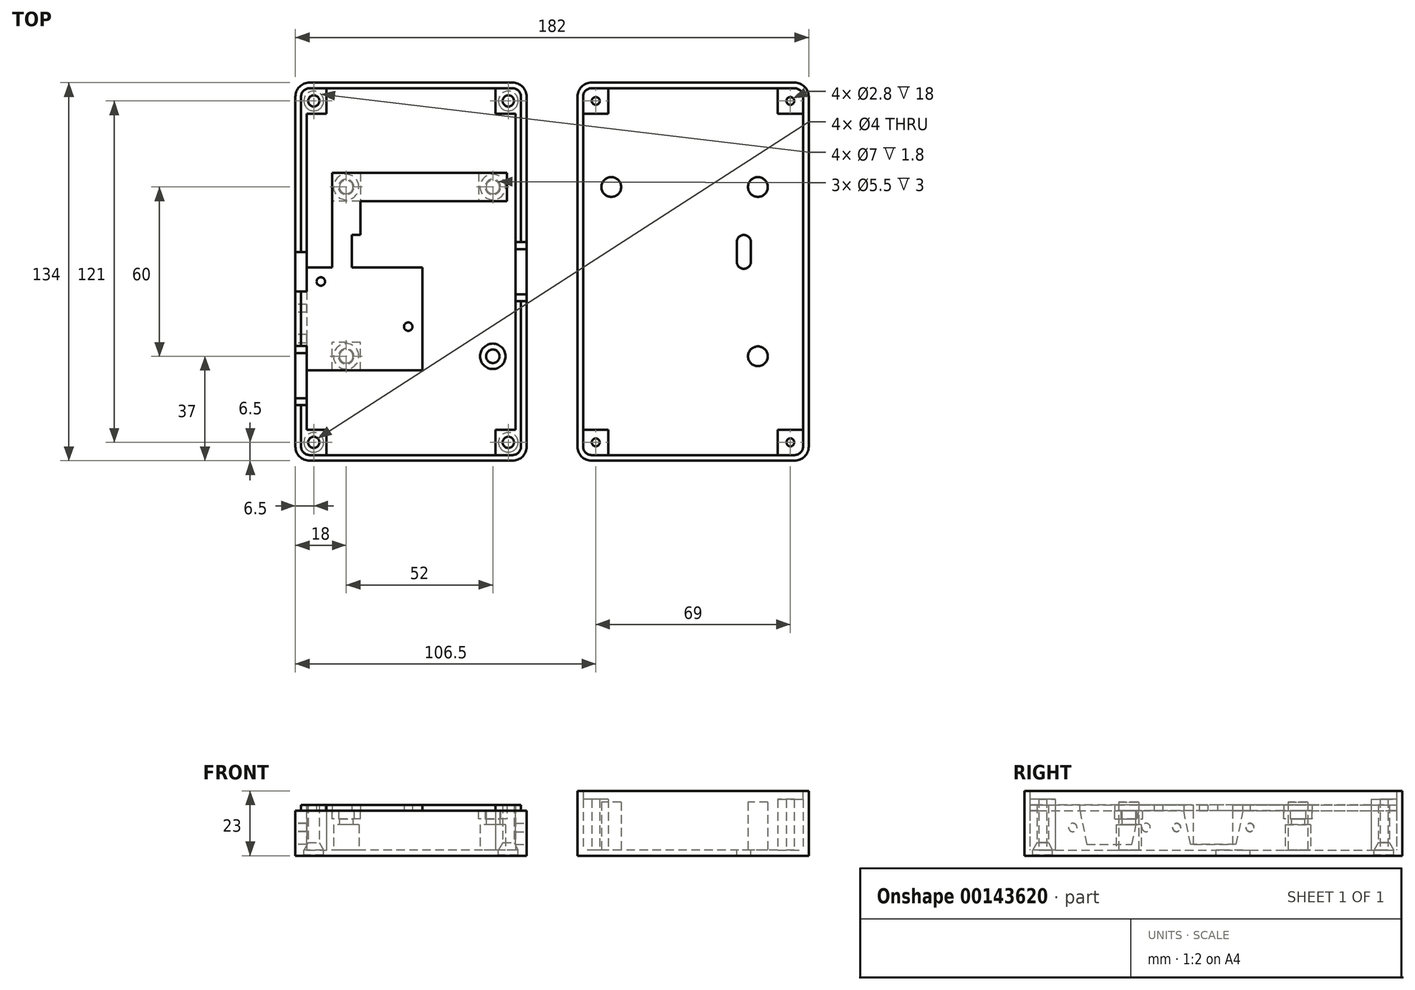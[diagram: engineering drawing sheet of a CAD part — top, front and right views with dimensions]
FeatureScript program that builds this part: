
annotation { "Feature Type Name" : "Feature", "Feature Type Description" : "" }
export const myFeature = defineFeature(function(context is Context, id is Id, definition is map)
    precondition{}
    {
        {
            var Q0;
            Q0=qCreatedBy(makeId("Top.planeOp"),FACE);
            var sketch = newSketch(context, id + "F0", { "sketchPlane" : qUnion([Q0])});
            skLineSegment(sketch, "E0.bottom", {"start": v(36, -67) * mm, "end": v(-36, -67) * mm});
            skLineSegment(sketch, "E0.top", {"start": v(36, 67) * mm, "end": v(-36, 67) * mm});
            skLineSegment(sketch, "E0.left", {"start": v(41, -62) * mm, "end": v(41, 62) * mm});
            skLineSegment(sketch, "E0.right", {"start": v(-41, -62) * mm, "end": v(-41, 62) * mm});
            skPoint(sketch, "E0.middle", {"position": v(0, 0) * mm});
            skPoint(sketch, "E1.visualSharp", {"position": v(41, 67) * mm});
            skArc(sketch, "E1.filletArc", {"start": v(41, 62) * mm, "mid": v(39.54, 65.54) * mm, "end": v(36, 67) * mm});
            skPoint(sketch, "E2.visualSharp", {"position": v(41, -67) * mm});
            skArc(sketch, "E2.filletArc", {"start": v(36, -67) * mm, "mid": v(39.54, -65.54) * mm, "end": v(41, -62) * mm});
            skPoint(sketch, "E3.visualSharp", {"position": v(-41, 67) * mm});
            skArc(sketch, "E3.filletArc", {"start": v(-36, 67) * mm, "mid": v(-39.54, 65.54) * mm, "end": v(-41, 62) * mm});
            skPoint(sketch, "E4.visualSharp", {"position": v(-41, -67) * mm});
            skArc(sketch, "E4.filletArc", {"start": v(-41, -62) * mm, "mid": v(-39.54, -65.54) * mm, "end": v(-36, -67) * mm});
            skSolve(sketch);
        }
        {
            var Q0;
            Q0 = qSketchRegion(id + "F0", true);
            extrude(context, id + "F1", {"entities" : qUnion([Q0]), "depth" : 16 * mm});
        }
        {
            var Q0;
            Q0=makeQuery(id+"F1.opExtrude","CAP_FACE",FACE,{"disambiguationData":[OSD([sQuery(id+"F0.wireOp",EDGE,"E0.bottom"),sQuery(id+"F0.wireOp",EDGE,"E0.top"),sQuery(id+"F0.wireOp",EDGE,"E0.left"),sQuery(id+"F0.wireOp",EDGE,"E0.right")])],"isStart":false});
            shell(context, id + "F2", {"entities" : qUnion([Q0]), "thickness" : 2 * mm});
        }
        {
            var Q0;
            Q0=makeQuery(id+"F2.opShell","OFFSET_FACE",FACE,{"disambiguationData":[OSD([sQuery(id+"F0.wireOp",EDGE,"E0.bottom"),sQuery(id+"F0.wireOp",EDGE,"E0.top"),sQuery(id+"F0.wireOp",EDGE,"E0.left"),sQuery(id+"F0.wireOp",EDGE,"E0.right")])]});
            var sketch = newSketch(context, id + "F3", { "sketchPlane" : qUnion([Q0])});
            skCircle(sketch, "E5", {"center": v(29, 30) * mm, "radius": 4.5 * mm});
            skCircle(sketch, "E6", {"center": v(-23, 30) * mm, "radius": 4.5 * mm});
            skCircle(sketch, "E7", {"center": v(29, -30) * mm, "radius": 4.5 * mm});
            skCircle(sketch, "E8", {"center": v(-23, -30) * mm, "radius": 4.5 * mm});
            skLineSegment(sketch, "E9.bottom", {"start": v(29, -21) * mm, "end": v(5, -21) * mm, "construction": true});
            skLineSegment(sketch, "E9.top", {"start": v(29, 21) * mm, "end": v(5, 21) * mm, "construction": true});
            skLineSegment(sketch, "E9.left", {"start": v(29, -21) * mm, "end": v(29, 21) * mm, "construction": true});
            skLineSegment(sketch, "E9.right", {"start": v(5, -21) * mm, "end": v(5, 21) * mm, "construction": true});
            skPoint(sketch, "E9.middle", {"position": v(17, 0) * mm});
            skCircle(sketch, "E10", {"center": v(9, -14.5) * mm, "radius": 1.4 * mm, "construction": true});
            skCircle(sketch, "E11", {"center": v(25, 14.5) * mm, "radius": 1.4 * mm, "construction": true});
            skLineSegment(sketch, "E12.bottom", {"start": v(21, 41) * mm, "end": v(-21, 41) * mm});
            skLineSegment(sketch, "E12.top", {"start": v(21, 65) * mm, "end": v(-21, 65) * mm});
            skLineSegment(sketch, "E12.left", {"start": v(21, 41) * mm, "end": v(21, 65) * mm});
            skLineSegment(sketch, "E12.right", {"start": v(-21, 41) * mm, "end": v(-21, 65) * mm});
            skPoint(sketch, "E12.middle", {"position": v(0, 53) * mm});
            skCircle(sketch, "E13", {"center": v(-14.5, 61) * mm, "radius": 1.5 * mm});
            skCircle(sketch, "E14", {"center": v(14.5, 45) * mm, "radius": 1.5 * mm});
            skLineSegment(sketch, "E15.bottom", {"start": v(39, -65) * mm, "end": v(30, -65) * mm});
            skLineSegment(sketch, "E15.top", {"start": v(39, -56) * mm, "end": v(30, -56) * mm});
            skLineSegment(sketch, "E15.left", {"start": v(39, -65) * mm, "end": v(39, -56) * mm});
            skLineSegment(sketch, "E15.right", {"start": v(30, -65) * mm, "end": v(30, -56) * mm});
            skPoint(sketch, "E15.middle", {"position": v(34.5, -60.5) * mm});
            skLineSegment(sketch, "E16.bottom", {"start": v(39, 56) * mm, "end": v(30, 56) * mm});
            skLineSegment(sketch, "E16.top", {"start": v(39, 65) * mm, "end": v(30, 65) * mm});
            skLineSegment(sketch, "E16.left", {"start": v(39, 56) * mm, "end": v(39, 65) * mm});
            skLineSegment(sketch, "E16.right", {"start": v(30, 56) * mm, "end": v(30, 65) * mm});
            skPoint(sketch, "E16.middle", {"position": v(34.5, 60.5) * mm});
            skLineSegment(sketch, "E17.MirrorCS", {"start": v(-30, -65) * mm, "end": v(-30, -56) * mm});
            skLineSegment(sketch, "E18.MirrorCS", {"start": v(-39, -65) * mm, "end": v(-30, -65) * mm});
            skLineSegment(sketch, "E19.MirrorCS", {"start": v(-39, -56) * mm, "end": v(-30, -56) * mm});
            skPoint(sketch, "E20.MirrorP", {"position": v(-34.5, -60.5) * mm});
            skLineSegment(sketch, "E21.MirrorCS", {"start": v(-39, -65) * mm, "end": v(-39, -56) * mm});
            skLineSegment(sketch, "E22.MirrorCS", {"start": v(-30, 56) * mm, "end": v(-30, 65) * mm});
            skLineSegment(sketch, "E23.MirrorCS", {"start": v(-39, 56) * mm, "end": v(-39, 65) * mm});
            skPoint(sketch, "E24.MirrorP", {"position": v(-34.5, 60.5) * mm});
            skLineSegment(sketch, "E25.MirrorCS", {"start": v(-39, 65) * mm, "end": v(-30, 65) * mm});
            skLineSegment(sketch, "E26.MirrorCS", {"start": v(-39, 56) * mm, "end": v(-30, 56) * mm});
            skSolve(sketch);
        }
        {
            var Q0;
            Q0=makeQuery(id+"F3.imprint","IMPRINT",FACE,{"disambiguationData":[TD([[makeQuery(id+"F3.imprint","IMPRINT",EDGE,{"derivedFrom":sQuery(id+"F3.wireOp",EDGE,"E6")}),1.0]])]});
            var Q1;
            Q1=makeQuery(id+"F3.imprint","IMPRINT",FACE,{"disambiguationData":[TD([[makeQuery(id+"F3.imprint","IMPRINT",EDGE,{"derivedFrom":sQuery(id+"F3.wireOp",EDGE,"E5")}),1.0]])]});
            var Q2;
            Q2=makeQuery(id+"F3.imprint","IMPRINT",FACE,{"disambiguationData":[TD([[makeQuery(id+"F3.imprint","IMPRINT",EDGE,{"derivedFrom":sQuery(id+"F3.wireOp",EDGE,"E7")}),1.0]])]});
            var Q3;
            Q3=makeQuery(id+"F3.imprint","IMPRINT",FACE,{"disambiguationData":[TD([[makeQuery(id+"F3.imprint","IMPRINT",EDGE,{"derivedFrom":sQuery(id+"F3.wireOp",EDGE,"E8")}),1.0]])]});
            extrude(context, id + "F4", {"entities" : qUnion([Q0, Q1, Q2, Q3]), "operationType" : NewBodyOperationType.ADD, "depth" : 9 * mm});
        }
        {
            var Q0;
            Q0=makeQuery(id+"F4.opExtrude","CAP_FACE",FACE,{"disambiguationData":[OSD([sQuery(id+"F3.wireOp",EDGE,"E6")])],"isStart":false});
            var Q1;
            Q1=makeQuery(id+"F4.opExtrude","CAP_FACE",FACE,{"disambiguationData":[OSD([sQuery(id+"F3.wireOp",EDGE,"E5")])],"isStart":false});
            cPlane(context, id + "F5", {"entities" : qUnion([Q0, Q1]), "cplaneType" : CPlaneType.MID_PLANE, "offset" : 17 * mm, "width" : 150 * mm, "height" : 150 * mm});
        }
        {
            var Q0;
            Q0=qCreatedBy(id+"F5.planeOp",FACE);
            var sketch = newSketch(context, id + "F6", { "sketchPlane" : qUnion([Q0])});
            skCircle(sketch, "E27", {"center": v(-23, 30) * mm, "radius": 2.4 * mm});
            skCircle(sketch, "E28", {"center": v(29, 30) * mm, "radius": 2.4 * mm});
            skCircle(sketch, "E29", {"center": v(29, -30) * mm, "radius": 2.4 * mm});
            skCircle(sketch, "E30", {"center": v(-23, -30) * mm, "radius": 2.4 * mm});
            skSolve(sketch);
        }
        {
            var Q0;
            Q0 = qSketchRegion(id + "F6", true);
            extrude(context, id + "F7", {"entities" : qUnion([Q0]), "operationType" : NewBodyOperationType.ADD, "depth" : 5 * mm});
        }
        {
            var Q0;
            Q0=makeQuery(id+"F1.opExtrude","SWEPT_FACE",FACE,{"disambiguationData":[OSD([sQuery(id+"F0.wireOp",EDGE,"E0.right")])]});
            var sketch = newSketch(context, id + "F8", { "sketchPlane" : qUnion([Q0])});
            skCircle(sketch, "E31", {"center": v(-13, 10) * mm, "radius": 1.4 * mm});
            skCircle(sketch, "E32", {"center": v(13, 10) * mm, "radius": 1.4 * mm});
            skLineSegment(sketch, "E33.bottom", {"start": v(7, 4) * mm, "end": v(-7, 4) * mm});
            skLineSegment(sketch, "E33.top", {"start": v(7, 16) * mm, "end": v(-7, 16) * mm});
            skLineSegment(sketch, "E33.left", {"start": v(7, 4) * mm, "end": v(7, 16) * mm});
            skLineSegment(sketch, "E33.right", {"start": v(-7, 4) * mm, "end": v(-7, 16) * mm});
            skPoint(sketch, "E33.middle", {"position": v(0, 10) * mm});
            skCircle(sketch, "E34", {"center": v(23.83, 10) * mm, "radius": 1.5 * mm});
            skCircle(sketch, "E35", {"center": v(49.83, 10) * mm, "radius": 1.5 * mm});
            skLineSegment(sketch, "E36", {"start": v(26.33, 16) * mm, "end": v(47.33, 16) * mm});
            skLineSegment(sketch, "E37", {"start": v(47.33, 16) * mm, "end": v(44.83, 4) * mm});
            skLineSegment(sketch, "E38", {"start": v(44.83, 4) * mm, "end": v(28.83, 4) * mm});
            skLineSegment(sketch, "E39", {"start": v(28.83, 4) * mm, "end": v(26.33, 16) * mm});
            skLineSegment(sketch, "E40.bottom", {"start": v(-7, 16) * mm, "end": v(7, 16) * mm});
            skLineSegment(sketch, "E40.top", {"start": v(-7, 18) * mm, "end": v(7, 18) * mm});
            skLineSegment(sketch, "E40.left", {"start": v(-7, 16) * mm, "end": v(-7, 18) * mm});
            skLineSegment(sketch, "E40.right", {"start": v(7, 16) * mm, "end": v(7, 18) * mm});
            skLineSegment(sketch, "E41.top", {"start": v(26.33, 18) * mm, "end": v(47.33, 18) * mm});
            skLineSegment(sketch, "E41.left", {"start": v(26.33, 16) * mm, "end": v(26.33, 18) * mm});
            skLineSegment(sketch, "E41.right", {"start": v(47.33, 16) * mm, "end": v(47.33, 18) * mm});
            skSolve(sketch);
        }
        {
            var Q0;
            Q0=makeQuery(id+"F1.opExtrude","SWEPT_FACE",FACE,{"disambiguationData":[OSD([sQuery(id+"F0.wireOp",EDGE,"E0.left")])]});
            var sketch = newSketch(context, id + "F9", { "sketchPlane" : qUnion([Q0])});
            skCircle(sketch, "E42", {"center": v(-13, 10) * mm, "radius": 1.5 * mm});
            skCircle(sketch, "E43", {"center": v(13, 10) * mm, "radius": 1.5 * mm});
            skLineSegment(sketch, "E44", {"start": v(-10.5, 16) * mm, "end": v(10.5, 16) * mm});
            skLineSegment(sketch, "E45", {"start": v(10.5, 16) * mm, "end": v(8, 4) * mm});
            skLineSegment(sketch, "E46", {"start": v(8, 4) * mm, "end": v(-8, 4) * mm});
            skLineSegment(sketch, "E47", {"start": v(-8, 4) * mm, "end": v(-10.5, 16) * mm});
            skLineSegment(sketch, "E48.top", {"start": v(-10.5, 18) * mm, "end": v(10.5, 18) * mm});
            skLineSegment(sketch, "E48.left", {"start": v(-10.5, 16) * mm, "end": v(-10.5, 18) * mm});
            skLineSegment(sketch, "E48.right", {"start": v(10.5, 16) * mm, "end": v(10.5, 18) * mm});
            skSolve(sketch);
        }
        {
            var Q0;
            Q0=makeQuery(id+"F3.imprint","IMPRINT",FACE,{"disambiguationData":[TD([[makeQuery(id+"F3.imprint","IMPRINT",EDGE,{"derivedFrom":sQuery(id+"F3.wireOp",EDGE,"E5")}),-1.0]])]});
            var sketch = newSketch(context, id + "F10", { "sketchPlane" : qUnion([Q0])});
            skLineSegment(sketch, "E49.bottom", {"start": v(-37, 56) * mm, "end": v(-39, 56) * mm});
            skLineSegment(sketch, "E49.top", {"start": v(-37, -56) * mm, "end": v(-39, -56) * mm});
            skLineSegment(sketch, "E49.left", {"start": v(-37, 56) * mm, "end": v(-37, -56) * mm});
            skLineSegment(sketch, "E49.right", {"start": v(-39, 56) * mm, "end": v(-39, -56) * mm});
            skLineSegment(sketch, "E50.bottom", {"start": v(39, 56) * mm, "end": v(37, 56) * mm});
            skLineSegment(sketch, "E50.top", {"start": v(39, -56) * mm, "end": v(37, -56) * mm});
            skLineSegment(sketch, "E50.left", {"start": v(39, 56) * mm, "end": v(39, -56) * mm});
            skLineSegment(sketch, "E50.right", {"start": v(37, 56) * mm, "end": v(37, -56) * mm});
            skSolve(sketch);
        }
        {
            var Q0;
            {var subQ3=sQuery(id+"F3.wireOp",EDGE,"E22.MirrorCS");Q0=makeQuery(id+"F3.imprint","IMPRINT",FACE,{"disambiguationData":[TD([[makeQuery(id+"F3.imprint","IMPRINT",EDGE,{"derivedFrom":subQ3}),1.0]])]});}
            var Q1;
            {var subQ4=sQuery(id+"F3.wireOp",EDGE,"E16.bottom");Q1=makeQuery(id+"F3.imprint","IMPRINT",FACE,{"disambiguationData":[TD([[makeQuery(id+"F3.imprint","IMPRINT",EDGE,{"derivedFrom":subQ4}),-1.0]])]});}
            var Q2;
            {var subQ1=sQuery(id+"F3.wireOp",EDGE,"E15.top");Q2=makeQuery(id+"F3.imprint","IMPRINT",FACE,{"disambiguationData":[TD([[makeQuery(id+"F3.imprint","IMPRINT",EDGE,{"derivedFrom":subQ1}),1.0]])]});}
            var Q3;
            {var subQ6=sQuery(id+"F3.wireOp",EDGE,"E17.MirrorCS");Q3=makeQuery(id+"F3.imprint","IMPRINT",FACE,{"disambiguationData":[TD([[makeQuery(id+"F3.imprint","IMPRINT",EDGE,{"derivedFrom":subQ6}),1.0]])]});}
            var Q4;
            Q4=makeQuery(id+"F10.imprint","IMPRINT",FACE,{"disambiguationData":[TD([[makeQuery(id+"F10.imprint","IMPRINT",EDGE,{"derivedFrom":sQuery(id+"F10.wireOp",EDGE,"E49.bottom")}),-1.0]])]});
            var Q5;
            Q5=makeQuery(id+"F10.imprint","IMPRINT",FACE,{"disambiguationData":[TD([[makeQuery(id+"F10.imprint","IMPRINT",EDGE,{"derivedFrom":sQuery(id+"F10.wireOp",EDGE,"E50.bottom")}),1.0]])]});
            extrude(context, id + "F11", {"entities" : qUnion([Q0, Q1, Q2, Q3, Q4, Q5]), "operationType" : NewBodyOperationType.ADD, "depth" : 16 * mm});
        }
        {
            var Q0;
            Q0 = qSketchRegion(id + "F9", true);
            extrude(context, id + "F12", {"entities" : qUnion([Q0]), "operationType" : NewBodyOperationType.REMOVE, "oppositeDirection" : true, "depth" : 4 * mm});
        }
        {
            var Q0;
            Q0 = qSketchRegion(id + "F8", true);
            extrude(context, id + "F13", {"entities" : qUnion([Q0]), "operationType" : NewBodyOperationType.REMOVE, "oppositeDirection" : true, "depth" : 4 * mm});
        }
        {
            var Q0;
            Q0=qCreatedBy(makeId("Top.planeOp"),FACE);
            var sketch = newSketch(context, id + "F14", { "sketchPlane" : qUnion([Q0])});
            skLineSegment(sketch, "E51.bottom", {"start": v(136, -67) * mm, "end": v(64, -67) * mm});
            skLineSegment(sketch, "E51.top", {"start": v(136, 67) * mm, "end": v(64, 67) * mm});
            skLineSegment(sketch, "E51.left", {"start": v(141, -62) * mm, "end": v(141, 62) * mm});
            skLineSegment(sketch, "E51.right", {"start": v(59, -62) * mm, "end": v(59, 62) * mm});
            skPoint(sketch, "E51.middle", {"position": v(100, 0) * mm});
            skPoint(sketch, "E52.visualSharp", {"position": v(59, 67) * mm});
            skArc(sketch, "E52.filletArc", {"start": v(64, 67) * mm, "mid": v(60.46, 65.54) * mm, "end": v(59, 62) * mm});
            skPoint(sketch, "E53.visualSharp", {"position": v(141, 67) * mm});
            skArc(sketch, "E53.filletArc", {"start": v(141, 62) * mm, "mid": v(139.54, 65.54) * mm, "end": v(136, 67) * mm});
            skPoint(sketch, "E54.visualSharp", {"position": v(59, -67) * mm});
            skArc(sketch, "E54.filletArc", {"start": v(59, -62) * mm, "mid": v(60.46, -65.54) * mm, "end": v(64, -67) * mm});
            skPoint(sketch, "E55.visualSharp", {"position": v(141, -67) * mm});
            skArc(sketch, "E55.filletArc", {"start": v(136, -67) * mm, "mid": v(139.54, -65.54) * mm, "end": v(141, -62) * mm});
            skSolve(sketch);
        }
        {
            var Q0;
            Q0 = qSketchRegion(id + "F14", true);
            extrude(context, id + "F15", {"entities" : qUnion([Q0]), "depth" : 23 * mm});
        }
        {
            var Q0;
            Q0=qCreatedBy(makeId("Right.planeOp"),FACE);
            cPlane(context, id + "F16", {"entities" : qUnion([Q0]), "cplaneType" : CPlaneType.OFFSET, "offset" : 100 * mm, "width" : 150 * mm, "height" : 150 * mm});
        }
        {
            var Q0;
            Q0=makeQuery(id+"F15.opExtrude","CAP_FACE",FACE,{"disambiguationData":[OSD([sQuery(id+"F14.wireOp",EDGE,"E51.bottom"),sQuery(id+"F14.wireOp",EDGE,"E51.top"),sQuery(id+"F14.wireOp",EDGE,"E51.left"),sQuery(id+"F14.wireOp",EDGE,"E51.right"),sQuery(id+"F14.wireOp",EDGE,"E52.filletArc"),sQuery(id+"F14.wireOp",EDGE,"E53.filletArc"),sQuery(id+"F14.wireOp",EDGE,"E54.filletArc"),sQuery(id+"F14.wireOp",EDGE,"E55.filletArc")])],"isStart":false});
            shell(context, id + "F17", {"entities" : qUnion([Q0]), "thickness" : 2 * mm});
        }
        {
            var Q0;
            Q0=makeQuery(id+"F17.opShell","OFFSET_FACE",FACE,{"disambiguationData":[OSD([sQuery(id+"F14.wireOp",EDGE,"E51.bottom"),sQuery(id+"F14.wireOp",EDGE,"E51.top"),sQuery(id+"F14.wireOp",EDGE,"E51.left"),sQuery(id+"F14.wireOp",EDGE,"E51.right"),sQuery(id+"F14.wireOp",EDGE,"E52.filletArc"),sQuery(id+"F14.wireOp",EDGE,"E53.filletArc"),sQuery(id+"F14.wireOp",EDGE,"E54.filletArc"),sQuery(id+"F14.wireOp",EDGE,"E55.filletArc")])]});
            var sketch = newSketch(context, id + "F18", { "sketchPlane" : qUnion([Q0])});
            skLineSegment(sketch, "E56.bottom", {"start": v(70, 56) * mm, "end": v(61, 56) * mm});
            skLineSegment(sketch, "E56.top", {"start": v(70, 65) * mm, "end": v(61, 65) * mm});
            skLineSegment(sketch, "E56.left", {"start": v(70, 56) * mm, "end": v(70, 65) * mm});
            skLineSegment(sketch, "E56.right", {"start": v(61, 56) * mm, "end": v(61, 65) * mm});
            skPoint(sketch, "E56.middle", {"position": v(65.5, 60.5) * mm});
            skCircle(sketch, "E57", {"center": v(65.5, 60.5) * mm, "radius": 1.4 * mm});
            skCircle(sketch, "E58", {"center": v(71, 30) * mm, "radius": 3.5 * mm});
            skCircle(sketch, "E59", {"center": v(123, 30) * mm, "radius": 3.5 * mm});
            skCircle(sketch, "E60", {"center": v(123, -30) * mm, "radius": 3.5 * mm});
            skCircle(sketch, "E61", {"center": v(71, -30) * mm, "radius": 3.5 * mm, "construction": true});
            skLineSegment(sketch, "E62.bottom", {"start": v(70, -56) * mm, "end": v(61, -56) * mm});
            skLineSegment(sketch, "E62.top", {"start": v(70, -65) * mm, "end": v(61, -65) * mm});
            skLineSegment(sketch, "E62.left", {"start": v(70, -56) * mm, "end": v(70, -65) * mm});
            skLineSegment(sketch, "E62.right", {"start": v(61, -56) * mm, "end": v(61, -65) * mm});
            skPoint(sketch, "E62.middle", {"position": v(65.5, -60.5) * mm});
            skCircle(sketch, "E63", {"center": v(65.5, -60.5) * mm, "radius": 1.4 * mm});
            skLineSegment(sketch, "E64.MirrorCS", {"start": v(130, -65) * mm, "end": v(139, -65) * mm});
            skLineSegment(sketch, "E65.MirrorCS", {"start": v(139, -56) * mm, "end": v(139, -65) * mm});
            skLineSegment(sketch, "E66.MirrorCS", {"start": v(130, -56) * mm, "end": v(130, -65) * mm});
            skCircle(sketch, "E67.MirrorC", {"center": v(134.5, -60.5) * mm, "radius": 1.4 * mm});
            skLineSegment(sketch, "E68.MirrorCS", {"start": v(130, -56) * mm, "end": v(139, -56) * mm});
            skLineSegment(sketch, "E69.MirrorCS", {"start": v(139, 56) * mm, "end": v(139, 65) * mm});
            skLineSegment(sketch, "E70.MirrorCS", {"start": v(130, 65) * mm, "end": v(139, 65) * mm});
            skLineSegment(sketch, "E71.MirrorCS", {"start": v(130, 56) * mm, "end": v(139, 56) * mm});
            skLineSegment(sketch, "E72.MirrorCS", {"start": v(130, 56) * mm, "end": v(130, 65) * mm});
            skCircle(sketch, "E73.MirrorC", {"center": v(134.5, 60.5) * mm, "radius": 1.4 * mm});
            skPoint(sketch, "E74.middle", {"position": v(118, 7) * mm});
            skLineSegment(sketch, "E75.left", {"start": v(120.5, 10.5) * mm, "end": v(120.5, 3.5) * mm});
            skLineSegment(sketch, "E75.right", {"start": v(115.5, 10.5) * mm, "end": v(115.5, 3.5) * mm});
            skArc(sketch, "E76", {"start": v(115.5, 10.5) * mm, "mid": v(118, 13) * mm, "end": v(120.5, 10.5) * mm});
            skArc(sketch, "E77", {"start": v(115.5, 3.5) * mm, "mid": v(118, 1) * mm, "end": v(120.5, 3.5) * mm});
            skLineSegment(sketch, "E78.bottom", {"start": v(108.78, -11.5) * mm, "end": v(91.12, -11.5) * mm, "construction": true});
            skPoint(sketch, "E78.middle", {"position": v(99.95, -13) * mm});
            skLineSegment(sketch, "E79.bottom", {"start": v(114.38, 1.5) * mm, "end": v(85.53, 1.5) * mm, "construction": true});
            skLineSegment(sketch, "E79.top", {"start": v(114.38, -1.5) * mm, "end": v(85.53, -1.5) * mm, "construction": true});
            skPoint(sketch, "E79.middle", {"position": v(99.95, 0) * mm});
            skLineSegment(sketch, "E80.top", {"start": v(108.78, 11.5) * mm, "end": v(91.12, 11.5) * mm, "construction": true});
            skPoint(sketch, "E80.middle", {"position": v(99.95, 13) * mm});
            skArc(sketch, "E81", {"start": v(87.86, 8) * mm, "mid": v(87.01, 6.54) * mm, "end": v(86.34, 5) * mm, "construction": true});
            skLineSegment(sketch, "E82.bottom", {"start": v(113.56, 5) * mm, "end": v(86.34, 5) * mm, "construction": true});
            skLineSegment(sketch, "E82.top", {"start": v(112.05, 8) * mm, "end": v(87.86, 8) * mm, "construction": true});
            skPoint(sketch, "E82.middle", {"position": v(99.95, 6.5) * mm});
            skLineSegment(sketch, "E83.bottom", {"start": v(112.05, -8) * mm, "end": v(87.86, -8) * mm, "construction": true});
            skLineSegment(sketch, "E83.top", {"start": v(113.56, -5) * mm, "end": v(86.34, -5) * mm, "construction": true});
            skPoint(sketch, "E83.middle", {"position": v(99.95, -6.5) * mm});
            skArc(sketch, "E84.trimOffspring", {"start": v(85.53, 1.5) * mm, "mid": v(85.45, 0) * mm, "end": v(85.53, -1.5) * mm, "construction": true});
            skArc(sketch, "E85.trimOffspring", {"start": v(86.34, -5) * mm, "mid": v(87.01, -6.54) * mm, "end": v(87.86, -8) * mm, "construction": true});
            skArc(sketch, "E86.trimOffspring", {"start": v(91.12, -11.5) * mm, "mid": v(99.95, -14.5) * mm, "end": v(108.78, -11.5) * mm, "construction": true});
            skArc(sketch, "E87.trimOffspring", {"start": v(112.05, -8) * mm, "mid": v(112.9, -6.54) * mm, "end": v(113.56, -5) * mm, "construction": true});
            skArc(sketch, "E88.trimOffspring", {"start": v(114.38, -1.5) * mm, "mid": v(114.45, 0) * mm, "end": v(114.38, 1.5) * mm, "construction": true});
            skArc(sketch, "E89.trimOffspring", {"start": v(113.56, 5) * mm, "mid": v(112.9, 6.54) * mm, "end": v(112.05, 8) * mm, "construction": true});
            skArc(sketch, "E90.trimOffspring", {"start": v(108.78, 11.5) * mm, "mid": v(99.95, 14.5) * mm, "end": v(91.12, 11.5) * mm, "construction": true});
            skSolve(sketch);
        }
        {
            var Q0;
            Q0=makeQuery(id+"F18.imprint","IMPRINT",FACE,{"disambiguationData":[TD([[makeQuery(id+"F18.imprint","IMPRINT",EDGE,{"derivedFrom":sQuery(id+"F18.wireOp",EDGE,"E59")}),1.0]])]});
            var Q1;
            Q1=makeQuery(id+"F18.imprint","IMPRINT",FACE,{"disambiguationData":[TD([[makeQuery(id+"F18.imprint","IMPRINT",EDGE,{"derivedFrom":sQuery(id+"F18.wireOp",EDGE,"E60")}),1.0]])]});
            var Q2;
            Q2=makeQuery(id+"F18.imprint","IMPRINT",FACE,{"disambiguationData":[TD([[makeQuery(id+"F18.imprint","IMPRINT",EDGE,{"derivedFrom":sQuery(id+"F18.wireOp",EDGE,"E61")}),1.0]])]});
            var Q3;
            Q3=makeQuery(id+"F18.imprint","IMPRINT",FACE,{"disambiguationData":[TD([[makeQuery(id+"F18.imprint","IMPRINT",EDGE,{"derivedFrom":sQuery(id+"F18.wireOp",EDGE,"E58")}),1.0]])]});
            extrude(context, id + "F19", {"entities" : qUnion([Q0, Q1, Q2, Q3]), "operationType" : NewBodyOperationType.ADD, "depth" : 17 * mm});
        }
        {
            var Q0;
            {var subQ6=sQuery(id+"F18.wireOp",EDGE,"E56.bottom");Q0=makeQuery(id+"F18.imprint","IMPRINT",FACE,{"disambiguationData":[TD([[makeQuery(id+"F18.imprint","IMPRINT",EDGE,{"derivedFrom":subQ6}),-1.0]])]});}
            var Q1;
            {var subQ5=sQuery(id+"F18.wireOp",EDGE,"E71.MirrorCS");Q1=makeQuery(id+"F18.imprint","IMPRINT",FACE,{"disambiguationData":[TD([[makeQuery(id+"F18.imprint","IMPRINT",EDGE,{"derivedFrom":subQ5}),1.0]])]});}
            var Q2;
            {var subQ6=sQuery(id+"F18.wireOp",EDGE,"E62.bottom");Q2=makeQuery(id+"F18.imprint","IMPRINT",FACE,{"disambiguationData":[TD([[makeQuery(id+"F18.imprint","IMPRINT",EDGE,{"derivedFrom":subQ6}),1.0]])]});}
            var Q3;
            {var subQ5=sQuery(id+"F18.wireOp",EDGE,"E66.MirrorCS");Q3=makeQuery(id+"F18.imprint","IMPRINT",FACE,{"disambiguationData":[TD([[makeQuery(id+"F18.imprint","IMPRINT",EDGE,{"derivedFrom":subQ5}),1.0]])]});}
            extrude(context, id + "F20", {"entities" : qUnion([Q0, Q1, Q2, Q3]), "operationType" : NewBodyOperationType.ADD, "depth" : 18 * mm});
        }
        {
            var Q0;
            Q0=sQuery(id+"F3.wireOp",VERTEX,"E20.MirrorP");
            var Q1;
            Q1=sQuery(id+"F3.wireOp",VERTEX,"E15.middle");
            var Q2;
            Q2=sQuery(id+"F3.wireOp",VERTEX,"E24.MirrorP");
            var Q3;
            Q3=sQuery(id+"F3.wireOp",VERTEX,"E16.middle");
            var Q4;
            Q4=makeQuery(id+"F1.opExtrude","SWEPT_BODY",BODY,{"disambiguationData":[OSD([sQuery(id+"F0.wireOp",EDGE,"E0.bottom"),sQuery(id+"F0.wireOp",EDGE,"E0.top"),sQuery(id+"F0.wireOp",EDGE,"E0.left"),sQuery(id+"F0.wireOp",EDGE,"E0.right"),sQuery(id+"F0.wireOp",EDGE,"E1.filletArc"),sQuery(id+"F0.wireOp",EDGE,"E2.filletArc"),sQuery(id+"F0.wireOp",EDGE,"E3.filletArc"),sQuery(id+"F0.wireOp",EDGE,"E4.filletArc")])]});
            hole(context, id + "F21", {"style" : HoleStyle.C_SINK, "endStyle" : HoleEndStyle.THROUGH, "oppositeDirection" : true, "holeDiameter" : 4 * mm, "cSinkDiameter" : 7 * mm, "cSinkAngle" : 60 * degree, "locations" : qUnion([Q0, Q1, Q2, Q3]), "scope" : qUnion([Q4]), "isTappedThrough" : true});
        }
        {
            var Q0;
            Q0=makeQuery(id+"F3.imprint","IMPRINT",FACE,{"disambiguationData":[TD([[makeQuery(id+"F3.imprint","IMPRINT",EDGE,{"derivedFrom":sQuery(id+"F3.wireOp",EDGE,"E5")}),-1.0]])]});
            var sketch = newSketch(context, id + "F22", { "sketchPlane" : qUnion([Q0])});
            skCircle(sketch, "E91", {"center": v(34.5, -60.5) * mm, "radius": 3.5 * mm});
            skCircle(sketch, "E92", {"center": v(34.5, 60.5) * mm, "radius": 3.5 * mm});
            skCircle(sketch, "E93.MirrorC", {"center": v(-34.5, -60.5) * mm, "radius": 3.5 * mm});
            skCircle(sketch, "E94.MirrorC", {"center": v(-34.5, 60.5) * mm, "radius": 3.5 * mm});
            skSolve(sketch);
        }
        {
            var Q0;
            Q0 = qSketchRegion(id + "F22", true);
            extrude(context, id + "F23", {"entities" : qUnion([Q0]), "operationType" : NewBodyOperationType.REMOVE, "oppositeDirection" : true, "depth" : 1.8 * mm});
        }
        {
            var Q0;
            Q0=makeQuery(id+"F7.opExtrude","CAP_FACE",FACE,{"disambiguationData":[OSD([sQuery(id+"F6.wireOp",EDGE,"E28")])],"isStart":false});
            var sketch = newSketch(context, id + "F24", { "sketchPlane" : qUnion([Q0])});
            skLineSegment(sketch, "E95.bottom", {"start": v(34, 35) * mm, "end": v(-28, 35) * mm});
            skLineSegment(sketch, "E95.top", {"start": v(34, 25) * mm, "end": v(-18, 25) * mm});
            skLineSegment(sketch, "E95.left", {"start": v(34, 35) * mm, "end": v(34, 25) * mm});
            skLineSegment(sketch, "E96.top", {"start": v(-28, -35) * mm, "end": v(-18, -35) * mm});
            skLineSegment(sketch, "E96.left", {"start": v(-28, 35) * mm, "end": v(-28, -35) * mm});
            skLineSegment(sketch, "E96.right", {"start": v(-18, 25) * mm, "end": v(-18, 13) * mm});
            skLineSegment(sketch, "E97.right", {"start": v(-18, 15) * mm, "end": v(-18, 13) * mm});
            skLineSegment(sketch, "E98.bottom", {"start": v(-18, 13) * mm, "end": v(-21, 13) * mm});
            skLineSegment(sketch, "E98.top", {"start": v(-18, 1.5) * mm, "end": v(-21, 1.5) * mm});
            skLineSegment(sketch, "E98.right", {"start": v(-21, 13) * mm, "end": v(-21, 1.5) * mm});
            skLineSegment(sketch, "E99.trimOffspring", {"start": v(-18, 1.5) * mm, "end": v(-18, -35) * mm});
            skLineSegment(sketch, "E100.bottom", {"start": v(4, 1.5) * mm, "end": v(-37, 1.5) * mm});
            skLineSegment(sketch, "E100.top", {"start": v(4, -35) * mm, "end": v(-37, -35) * mm});
            skLineSegment(sketch, "E100.left", {"start": v(4, 1.5) * mm, "end": v(4, -35) * mm});
            skLineSegment(sketch, "E100.right", {"start": v(-37, 1.5) * mm, "end": v(-37, -35) * mm});
            skCircle(sketch, "E101", {"center": v(-1, -19.5) * mm, "radius": 1.5 * mm});
            skCircle(sketch, "E102", {"center": v(-32, -3.5) * mm, "radius": 1.5 * mm});
            skSolve(sketch);
        }
        {
            var Q0;
            Q0 = qSketchRegion(id + "F24", true);
            extrude(context, id + "F25", {"entities" : qUnion([Q0]), "depth" : 2 * mm});
        }
        {
            var Q0;
            Q0=makeQuery(id+"F25.opExtrude","CAP_FACE",FACE,{"disambiguationData":[OSD([sQuery(id+"F24.wireOp",EDGE,"E95.bottom"),sQuery(id+"F24.wireOp",EDGE,"E95.top"),sQuery(id+"F24.wireOp",EDGE,"E95.left"),sQuery(id+"F24.wireOp",EDGE,"E96.left"),sQuery(id+"F24.wireOp",EDGE,"E96.right"),sQuery(id+"F24.wireOp",EDGE,"E97.right"),sQuery(id+"F24.wireOp",EDGE,"E98.bottom"),sQuery(id+"F24.wireOp",EDGE,"E98.right"),sQuery(id+"F24.wireOp",EDGE,"E100.bottom"),sQuery(id+"F24.wireOp",EDGE,"E100.top"),sQuery(id+"F24.wireOp",EDGE,"E100.left"),sQuery(id+"F24.wireOp",EDGE,"E100.right"),sQuery(id+"F24.wireOp",EDGE,"E101"),sQuery(id+"F24.wireOp",EDGE,"E102")])],"isStart":true});
            var sketch = newSketch(context, id + "F26", { "sketchPlane" : qUnion([Q0])});
            skLineSegment(sketch, "E103.bottom", {"start": v(34, -35) * mm, "end": v(24, -35) * mm});
            skLineSegment(sketch, "E103.top", {"start": v(34, -25) * mm, "end": v(24, -25) * mm});
            skLineSegment(sketch, "E103.left", {"start": v(34, -35) * mm, "end": v(34, -25) * mm});
            skLineSegment(sketch, "E103.right", {"start": v(24, -35) * mm, "end": v(24, -25) * mm});
            skLineSegment(sketch, "E104.bottom", {"start": v(34, -35) * mm, "end": v(34, -35) * mm});
            skLineSegment(sketch, "E104.top", {"start": v(34, -25) * mm, "end": v(34, -25) * mm});
            skLineSegment(sketch, "E105.bottom", {"start": v(-18, -35) * mm, "end": v(-28, -35) * mm});
            skLineSegment(sketch, "E105.top", {"start": v(-18, -25) * mm, "end": v(-28, -25) * mm});
            skLineSegment(sketch, "E105.left", {"start": v(-18, -35) * mm, "end": v(-18, -25) * mm});
            skLineSegment(sketch, "E105.right", {"start": v(-28, -35) * mm, "end": v(-28, -25) * mm});
            skLineSegment(sketch, "E106.bottom", {"start": v(-18, 35) * mm, "end": v(-28, 35) * mm});
            skLineSegment(sketch, "E106.top", {"start": v(-18, 25) * mm, "end": v(-28, 25) * mm});
            skLineSegment(sketch, "E106.left", {"start": v(-18, 35) * mm, "end": v(-18, 25) * mm});
            skLineSegment(sketch, "E106.right", {"start": v(-28, 35) * mm, "end": v(-28, 25) * mm});
            skPoint(sketch, "E106.middle", {"position": v(-23, 30) * mm});
            skSolve(sketch);
        }
        {
            var Q0;
            Q0 = qSketchRegion(id + "F26", true);
            extrude(context, id + "F27", {"entities" : qUnion([Q0]), "operationType" : NewBodyOperationType.ADD, "depth" : 3 * mm});
        }
        {
            var Q0;
            Q0=makeQuery(id+"F27.opExtrude","CAP_FACE",FACE,{"disambiguationData":[OSD([sQuery(id+"F26.wireOp",EDGE,"E105.bottom"),sQuery(id+"F26.wireOp",EDGE,"E105.top"),sQuery(id+"F26.wireOp",EDGE,"E105.left"),sQuery(id+"F26.wireOp",EDGE,"E105.right")])],"isStart":false});
            var sketch = newSketch(context, id + "F28", { "sketchPlane" : qUnion([Q0])});
            skCircle(sketch, "E107", {"center": v(-23, 30) * mm, "radius": 2.75 * mm});
            skCircle(sketch, "E108", {"center": v(-23, -30) * mm, "radius": 2.75 * mm});
            skCircle(sketch, "E109", {"center": v(29, -30) * mm, "radius": 2.75 * mm});
            skSolve(sketch);
        }
        {
            var Q0;
            Q0 = qSketchRegion(id + "F28", true);
            extrude(context, id + "F29", {"entities" : qUnion([Q0]), "operationType" : NewBodyOperationType.REMOVE, "oppositeDirection" : true, "depth" : 3 * mm});
        }
        {
            var Q0;
            Q0=makeQuery(id+"F18.imprint","IMPRINT",FACE,{"disambiguationData":[TD([[makeQuery(id+"F18.imprint","IMPRINT",EDGE,{"derivedFrom":sQuery(id+"F18.wireOp",EDGE,"E75.left")}),-1.0]])]});
            var Q1;
            Q1=makeQuery(id+"F18.imprint","IMPRINT",FACE,{"disambiguationData":[TD([[makeQuery(id+"F18.imprint","IMPRINT",EDGE,{"derivedFrom":sQuery(id+"F18.wireOp",EDGE,"E78.bottom")}),1.0]])]});
            var Q2;
            Q2=makeQuery(id+"F18.imprint","IMPRINT",FACE,{"disambiguationData":[TD([[makeQuery(id+"F18.imprint","IMPRINT",EDGE,{"derivedFrom":sQuery(id+"F18.wireOp",EDGE,"E83.bottom")}),-1.0]])]});
            var Q3;
            Q3=makeQuery(id+"F18.imprint","IMPRINT",FACE,{"disambiguationData":[TD([[makeQuery(id+"F18.imprint","IMPRINT",EDGE,{"derivedFrom":sQuery(id+"F18.wireOp",EDGE,"E79.bottom")}),1.0]])]});
            var Q4;
            Q4=makeQuery(id+"F18.imprint","IMPRINT",FACE,{"disambiguationData":[TD([[makeQuery(id+"F18.imprint","IMPRINT",EDGE,{"derivedFrom":sQuery(id+"F18.wireOp",EDGE,"E81")}),1.0]])]});
            var Q5;
            Q5=makeQuery(id+"F18.imprint","IMPRINT",FACE,{"disambiguationData":[TD([[makeQuery(id+"F18.imprint","IMPRINT",EDGE,{"derivedFrom":sQuery(id+"F18.wireOp",EDGE,"E80.top")}),-1.0]])]});
            extrude(context, id + "F30", {"entities" : qUnion([Q0, Q1, Q2, Q3, Q4, Q5]), "operationType" : NewBodyOperationType.REMOVE, "oppositeDirection" : true, "depth" : 2 * mm});
        }
    });
